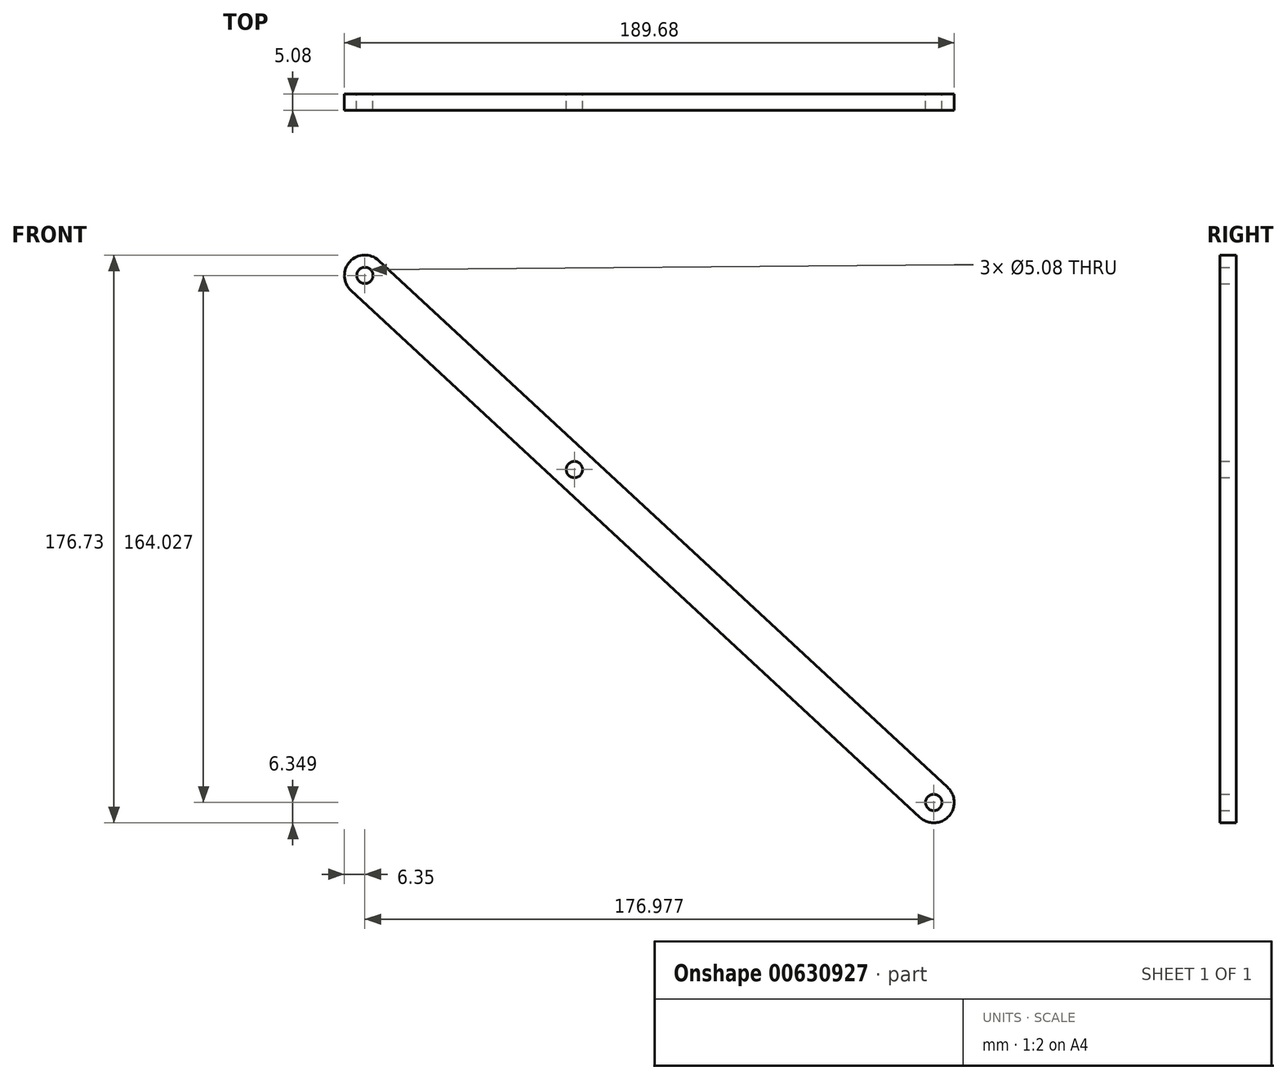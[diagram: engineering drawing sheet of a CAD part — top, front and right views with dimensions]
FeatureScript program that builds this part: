
annotation { "Feature Type Name" : "Feature", "Feature Type Description" : "" }
export const myFeature = defineFeature(function(context is Context, id is Id, definition is map)
    precondition{}
    {
        {
            var Q0;
            Q0=qCreatedBy(makeId("Front.planeOp"),FACE);
            var sketch = newSketch(context, id + "F0", { "sketchPlane" : qUnion([Q0])});
            skCircle(sketch, "E0", {"center": v(-73.98, 46.19) * mm, "radius": 6.35 * mm});
            skCircle(sketch, "E1", {"center": v(-73.98, 46.19) * mm, "radius": 2.54 * mm});
            skCircle(sketch, "E2", {"center": v(-8.78, -14.25) * mm, "radius": 6.35 * mm});
            skCircle(sketch, "E3", {"center": v(-8.78, -14.25) * mm, "radius": 2.54 * mm});
            skCircle(sketch, "E4", {"center": v(103, -117.84) * mm, "radius": 6.35 * mm});
            skCircle(sketch, "E5", {"center": v(103, -117.84) * mm, "radius": 2.54 * mm});
            skLineSegment(sketch, "E6", {"start": v(-78.3, 41.53) * mm, "end": v(98.68, -122.5) * mm});
            skLineSegment(sketch, "E7", {"start": v(-69.66, 50.84) * mm, "end": v(107.31, -113.18) * mm});
            skSolve(sketch);
        }
        {
            var Q0;
            Q0 = qSketchRegion(id + "F0", true);
            extrude(context, id + "F1", {"entities" : qUnion([Q0]), "depth" : 5.08 * mm, "offsetDistance" : 25.4 * mm});
        }
    });
